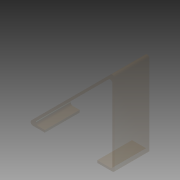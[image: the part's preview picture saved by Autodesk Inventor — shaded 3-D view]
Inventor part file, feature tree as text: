
AUTODESK INVENTOR PART (.ipt)
format: ipt  version: 2012 (Build 160160000, 160)  size: 96,768 bytes
history: native  units: in
note: dims shown in document units (in); Inventor stores cm internally (conversion verified against a paired STEP export)
features: extrude x1, fillet x1, sketch x1
ambient origin geometry x8: Origin, YZ Plane, XZ Plane, XY Plane, X Axis, Y Axis, Z Axis, Center Point
bodies: Solid1 (feature_tree)
feature tree (3):
  extrude  "Extrusion1"  Depth=5.0in
  fillet  "Fillet1"  Radius=1.0in
  sketch  "Sketch1"  dims[d0=5.0in d1=5.0in d2=1.0in d4=0.125in d5=0.125in d6=0.125in d7=1.0in d8=0.125in d9=2.0in d10=0.0in d11=0.125in]
